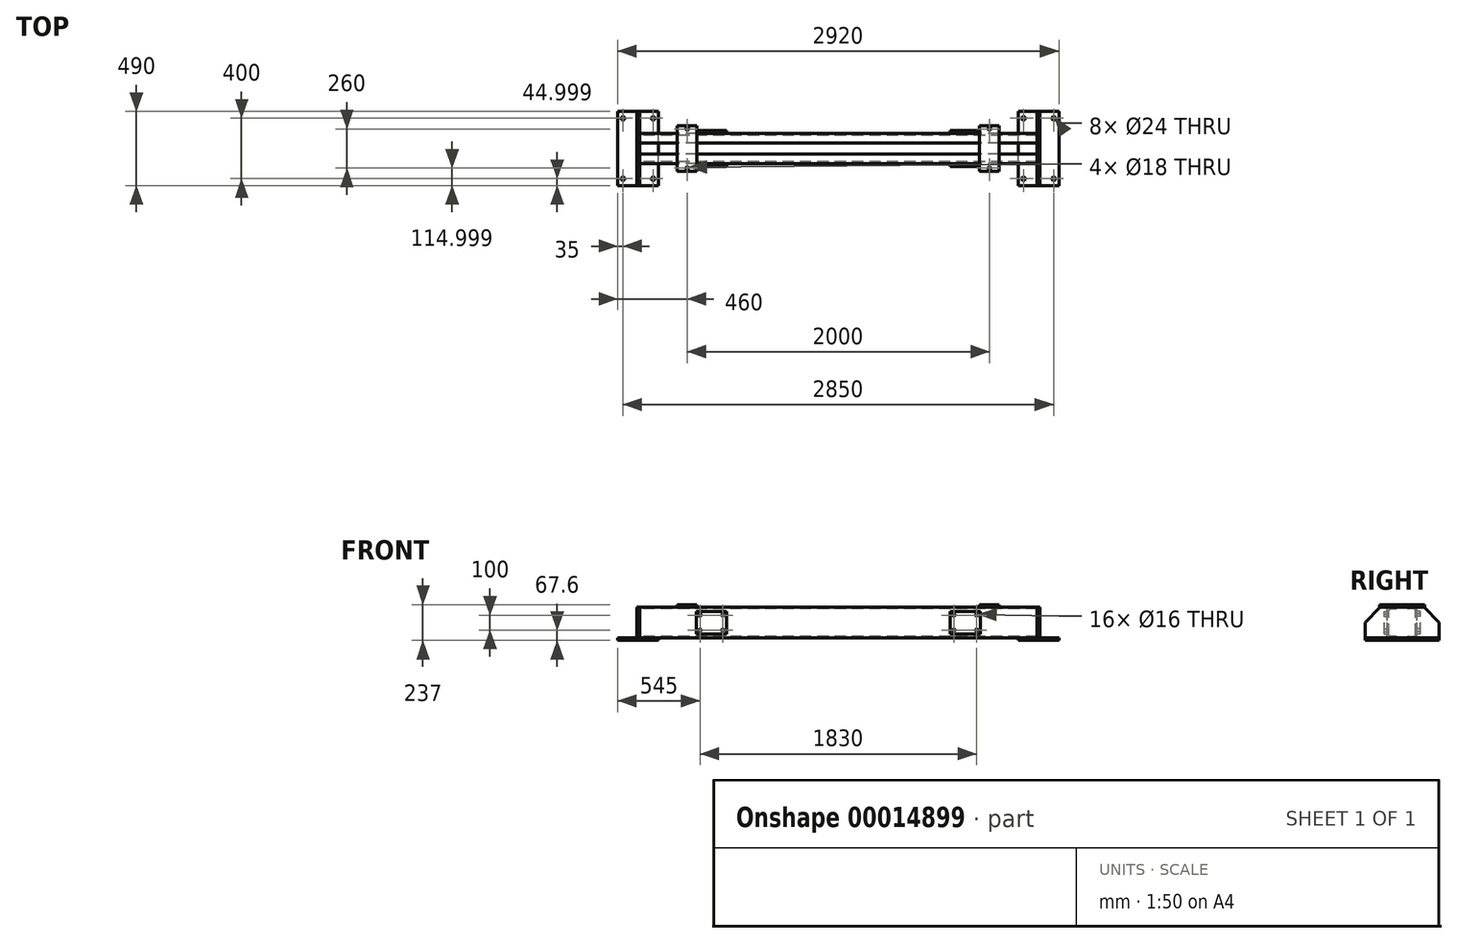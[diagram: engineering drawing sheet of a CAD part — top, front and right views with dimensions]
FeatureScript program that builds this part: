
annotation { "Feature Type Name" : "Feature", "Feature Type Description" : "" }
export const myFeature = defineFeature(function(context is Context, id is Id, definition is map)
    precondition{}
    {
        {
            var Q0;
            Q0=qCreatedBy(makeId("Right.planeOp"),FACE);
            var sketch = newSketch(context, id + "F0", { "sketchPlane" : qUnion([Q0])});
            skLineSegment(sketch, "E0", {"start": v(-32.03, -101.6) * mm, "end": v(-32.03, 101.6) * mm});
            skLineSegment(sketch, "E1", {"start": v(-32.03, 101.6) * mm, "end": v(32.03, 101.6) * mm});
            skLineSegment(sketch, "E2", {"start": v(32.03, 96.65) * mm, "end": v(32.03, 101.6) * mm});
            skArc(sketch, "E3", {"start": v(27.08, 91.7) * mm, "mid": v(30.58, 93.14) * mm, "end": v(32.03, 96.65) * mm});
            skLineSegment(sketch, "E4", {"start": v(-9.46, 91.7) * mm, "end": v(27.08, 91.7) * mm});
            skArc(sketch, "E5", {"start": v(-9.46, 91.7) * mm, "mid": v(-16.64, 88.71) * mm, "end": v(-19.62, 81.53) * mm});
            skLineSegment(sketch, "E6", {"start": v(-19.62, -81.53) * mm, "end": v(-19.62, 81.53) * mm});
            skArc(sketch, "E7", {"start": v(-19.62, -81.53) * mm, "mid": v(-16.64, -88.71) * mm, "end": v(-9.46, -91.7) * mm});
            skLineSegment(sketch, "E8", {"start": v(27.08, -91.7) * mm, "end": v(-9.46, -91.7) * mm});
            skArc(sketch, "E9", {"start": v(32.03, -96.65) * mm, "mid": v(30.58, -93.14) * mm, "end": v(27.08, -91.7) * mm});
            skLineSegment(sketch, "E10", {"start": v(32.03, -101.6) * mm, "end": v(32.03, -96.65) * mm});
            skLineSegment(sketch, "E11", {"start": v(-32.03, -101.6) * mm, "end": v(32.03, -101.6) * mm});
            skSolve(sketch);
        }
        {
            var Q0;
            Q0 = qSketchRegion(id + "F0", true);
            extrude(context, id + "F1", {"entities" : qUnion([Q0]), "endBound" : BoundingType.SYMMETRIC, "depth" : 2631 * mm});
        }
        {
            var Q0;
            Q0=makeQuery(id+"F1.opExtrude","SWEPT_FACE",FACE,{"disambiguationData":[OSD([sQuery(id+"F0.wireOp",EDGE,"E0")])]});
            cPlane(context, id + "F2", {"entities" : qUnion([Q0]), "cplaneType" : CPlaneType.OFFSET, "offset" : 100 * mm, "oppositeDirection" : true, "width" : 150 * mm, "height" : 150 * mm});
        }
        {
            var Q0;
            Q0=makeQuery(id+"F1.opExtrude","SWEPT_BODY",BODY,{"disambiguationData":[OSD([sQuery(id+"F0.wireOp",EDGE,"E0"),sQuery(id+"F0.wireOp",EDGE,"E1"),sQuery(id+"F0.wireOp",EDGE,"E2"),sQuery(id+"F0.wireOp",EDGE,"E3"),sQuery(id+"F0.wireOp",EDGE,"E4"),sQuery(id+"F0.wireOp",EDGE,"E5"),sQuery(id+"F0.wireOp",EDGE,"E6"),sQuery(id+"F0.wireOp",EDGE,"E7"),sQuery(id+"F0.wireOp",EDGE,"E8"),sQuery(id+"F0.wireOp",EDGE,"E9"),sQuery(id+"F0.wireOp",EDGE,"E10"),sQuery(id+"F0.wireOp",EDGE,"E11")])]});
            var Q1;
            Q1=qCreatedBy(id+"F2.planeOp",FACE);
            mirror(context, id + "F3", {"entities" : qUnion([Q0]), "mirrorPlane" : qUnion([Q1])});
        }
        {
            var Q0;
            Q0=makeQuery(id+"F1.opExtrude","CAP_FACE",FACE,{"disambiguationData":[OSD([sQuery(id+"F0.wireOp",EDGE,"E0"),sQuery(id+"F0.wireOp",EDGE,"E1"),sQuery(id+"F0.wireOp",EDGE,"E2"),sQuery(id+"F0.wireOp",EDGE,"E3"),sQuery(id+"F0.wireOp",EDGE,"E4"),sQuery(id+"F0.wireOp",EDGE,"E5"),sQuery(id+"F0.wireOp",EDGE,"E6"),sQuery(id+"F0.wireOp",EDGE,"E7"),sQuery(id+"F0.wireOp",EDGE,"E8"),sQuery(id+"F0.wireOp",EDGE,"E9"),sQuery(id+"F0.wireOp",EDGE,"E10"),sQuery(id+"F0.wireOp",EDGE,"E11")])],"isStart":false});
            var sketch = newSketch(context, id + "F4", { "sketchPlane" : qUnion([Q0])});
            skLineSegment(sketch, "E12.0", {"start": v(167.97, -101.6) * mm, "end": v(167.97, 101.6) * mm, "construction": true});
            skLineSegment(sketch, "E13.0", {"start": v(-32.03, -101.6) * mm, "end": v(-32.03, 101.6) * mm, "construction": true});
            skLineSegment(sketch, "E14", {"start": v(-32.03, 0) * mm, "end": v(167.97, 0) * mm, "construction": true});
            skLineSegment(sketch, "E15", {"start": v(67.97, 0) * mm, "end": v(67.97, -135.85) * mm, "construction": true});
            skLineSegment(sketch, "E16.0.0", {"start": v(-32.03, 101.6) * mm, "end": v(-32.03, -101.6) * mm, "construction": true});
            skLineSegment(sketch, "E16.0.1", {"start": v(-32.03, -101.6) * mm, "end": v(32.03, -101.6) * mm, "construction": true});
            skLineSegment(sketch, "E16.0.2", {"start": v(32.03, -101.6) * mm, "end": v(32.03, -96.65) * mm, "construction": true});
            skArc(sketch, "E16.0.3", {"start": v(32.03, -96.65) * mm, "mid": v(30.58, -93.14) * mm, "end": v(27.08, -91.7) * mm, "construction": true});
            skLineSegment(sketch, "E16.0.4", {"start": v(27.08, -91.7) * mm, "end": v(-9.46, -91.7) * mm, "construction": true});
            skArc(sketch, "E16.0.5", {"start": v(-9.46, -91.7) * mm, "mid": v(-16.64, -88.71) * mm, "end": v(-19.62, -81.53) * mm, "construction": true});
            skLineSegment(sketch, "E16.0.6", {"start": v(-19.62, -81.53) * mm, "end": v(-19.62, 81.53) * mm, "construction": true});
            skArc(sketch, "E16.0.7", {"start": v(-19.62, 81.53) * mm, "mid": v(-16.64, 88.71) * mm, "end": v(-9.46, 91.7) * mm, "construction": true});
            skLineSegment(sketch, "E16.0.8", {"start": v(-9.46, 91.7) * mm, "end": v(27.08, 91.7) * mm, "construction": true});
            skArc(sketch, "E16.0.9", {"start": v(27.08, 91.7) * mm, "mid": v(30.58, 93.14) * mm, "end": v(32.03, 96.65) * mm, "construction": true});
            skLineSegment(sketch, "E16.0.10", {"start": v(32.03, 96.65) * mm, "end": v(32.03, 101.6) * mm, "construction": true});
            skLineSegment(sketch, "E16.0.11", {"start": v(32.03, 101.6) * mm, "end": v(-32.03, 101.6) * mm, "construction": true});
            skLineSegment(sketch, "E17.0.1", {"start": v(167.97, 101.6) * mm, "end": v(103.9, 101.6) * mm, "construction": true});
            skLineSegment(sketch, "E17.0.2", {"start": v(103.9, 101.6) * mm, "end": v(103.9, 96.65) * mm, "construction": true});
            skArc(sketch, "E17.0.3", {"start": v(103.9, 96.65) * mm, "mid": v(105.36, 93.14) * mm, "end": v(108.86, 91.7) * mm, "construction": true});
            skLineSegment(sketch, "E17.0.4", {"start": v(108.86, 91.7) * mm, "end": v(145.4, 91.7) * mm, "construction": true});
            skArc(sketch, "E17.0.5", {"start": v(145.4, 91.7) * mm, "mid": v(152.58, 88.71) * mm, "end": v(155.56, 81.53) * mm, "construction": true});
            skLineSegment(sketch, "E17.0.6", {"start": v(155.56, 81.53) * mm, "end": v(155.56, -81.53) * mm, "construction": true});
            skArc(sketch, "E17.0.7", {"start": v(155.56, -81.53) * mm, "mid": v(152.58, -88.71) * mm, "end": v(145.4, -91.7) * mm, "construction": true});
            skLineSegment(sketch, "E17.0.8", {"start": v(145.4, -91.7) * mm, "end": v(108.86, -91.7) * mm, "construction": true});
            skArc(sketch, "E17.0.9", {"start": v(108.86, -91.7) * mm, "mid": v(105.36, -93.14) * mm, "end": v(103.9, -96.65) * mm, "construction": true});
            skLineSegment(sketch, "E17.0.10", {"start": v(103.9, -96.65) * mm, "end": v(103.9, -101.6) * mm, "construction": true});
            skLineSegment(sketch, "E17.0.11", {"start": v(103.9, -101.6) * mm, "end": v(167.97, -101.6) * mm, "construction": true});
            skLineSegment(sketch, "E18.0", {"start": v(-177.03, 0) * mm, "end": v(-177.03, -101.6) * mm, "construction": true});
            skLineSegment(sketch, "E19.MirrorCS", {"start": v(312.97, 101.6) * mm, "end": v(312.97, -101.6) * mm});
            skPoint(sketch, "E20.orphan", {"position": v(312.97, 0) * mm});
            skLineSegment(sketch, "E21.bottom", {"start": v(312.97, 101.6) * mm, "end": v(-177.03, 101.6) * mm});
            skLineSegment(sketch, "E21.top", {"start": v(312.97, -101.6) * mm, "end": v(-177.03, -101.6) * mm});
            skLineSegment(sketch, "E21.right", {"start": v(-177.03, 101.6) * mm, "end": v(-177.03, -101.6) * mm});
            skSolve(sketch);
        }
        {
            var Q0;
            Q0 = qSketchRegion(id + "F4", true);
            extrude(context, id + "F5", {"entities" : qUnion([Q0]), "depth" : 19 * mm});
        }
        {
            var Q0;
            Q0=makeQuery(id+"F5.opExtrude","SWEPT_EDGE",EDGE,{"disambiguationData":[OSD([sQuery(id+"F4.wireOp",EDGE,"E21.bottom"),sQuery(id+"F4.wireOp",EDGE,"E21.right")])]});
            var Q1;
            Q1=makeQuery(id+"F5.opExtrude","SWEPT_EDGE",EDGE,{"disambiguationData":[OSD([sQuery(id+"F4.wireOp",EDGE,"E21.bottom"),sQuery(id+"F4.wireOp",EDGE,"E19.MirrorCS")])]});
            chamfer(context, id + "F6", {"entities" : qUnion([Q0, Q1]), "width" : 100 * mm, "tangentPropagation" : true});
        }
        {
            var Q0;
            Q0=makeQuery(id+"F5.opExtrude","SWEPT_BODY",BODY,{"disambiguationData":[OSD([sQuery(id+"F4.wireOp",EDGE,"E21.bottom"),sQuery(id+"F4.wireOp",EDGE,"E21.top"),sQuery(id+"F4.wireOp",EDGE,"E19.MirrorCS"),sQuery(id+"F4.wireOp",EDGE,"E21.right")])]});
            var Q1;
            Q1=qCreatedBy(makeId("Right.planeOp"),FACE);
            mirror(context, id + "F7", {"entities" : qUnion([Q0]), "mirrorPlane" : qUnion([Q1])});
        }
        {
            var Q0;
            Q0=makeQuery(id+"F7.opPattern","COPY",FACE,{"derivedFrom":makeQuery(id+"F5.opExtrude","SWEPT_FACE",FACE,{"disambiguationData":[OSD([sQuery(id+"F4.wireOp",EDGE,"E21.top")])]}),"instanceName":"1"});
            var sketch = newSketch(context, id + "F8", { "sketchPlane" : qUnion([Q0])});
            skLineSegment(sketch, "E22", {"start": v(-1325, 177.03) * mm, "end": v(-1325, -312.97) * mm, "construction": true});
            skLineSegment(sketch, "E23.0", {"start": v(-1460, 177.03) * mm, "end": v(-1460, -312.97) * mm});
            skLineSegment(sketch, "E24", {"start": v(-1460, 177.03) * mm, "end": v(-1325, 177.03) * mm});
            skLineSegment(sketch, "E25", {"start": v(-1460, -312.97) * mm, "end": v(-1325, -312.97) * mm});
            skLineSegment(sketch, "E26.MirrorCS", {"start": v(-1190, 177.03) * mm, "end": v(-1325, 177.03) * mm});
            skLineSegment(sketch, "E27.MirrorCS", {"start": v(-1190, 177.03) * mm, "end": v(-1190, -312.97) * mm});
            skLineSegment(sketch, "E28.MirrorCS", {"start": v(-1190, -312.97) * mm, "end": v(-1325, -312.97) * mm});
            skLineSegment(sketch, "E29", {"start": v(-1190, -67.97) * mm, "end": v(-1460, -67.97) * mm, "construction": true});
            skLineSegment(sketch, "E30.0", {"start": v(-1425, 177.03) * mm, "end": v(-1425, -312.97) * mm, "construction": true});
            skLineSegment(sketch, "E31.0", {"start": v(-1190, -267.97) * mm, "end": v(-1460, -267.97) * mm, "construction": true});
            skCircle(sketch, "E32", {"center": v(-1425, -267.97) * mm, "radius": 12 * mm});
            skCircle(sketch, "E33.MirrorC", {"center": v(-1225, -267.97) * mm, "radius": 12 * mm});
            skCircle(sketch, "E34.MirrorC", {"center": v(-1225, 132.03) * mm, "radius": 12 * mm});
            skCircle(sketch, "E35.MirrorC", {"center": v(-1425, 132.03) * mm, "radius": 12 * mm});
            skSolve(sketch);
        }
        {
            var Q0;
            Q0 = qSketchRegion(id + "F8", true);
            extrude(context, id + "F9", {"entities" : qUnion([Q0]), "depth" : 16 * mm});
        }
        {
            var Q0;
            Q0=makeQuery(id+"F9.opExtrude","SWEPT_BODY",BODY,{"disambiguationData":[OSD([sQuery(id+"F8.wireOp",EDGE,"E23.0"),sQuery(id+"F8.wireOp",EDGE,"E24"),sQuery(id+"F8.wireOp",EDGE,"E25"),sQuery(id+"F8.wireOp",EDGE,"E26.MirrorCS"),sQuery(id+"F8.wireOp",EDGE,"E27.MirrorCS"),sQuery(id+"F8.wireOp",EDGE,"E28.MirrorCS"),sQuery(id+"F8.wireOp",EDGE,"E32"),sQuery(id+"F8.wireOp",EDGE,"E33.MirrorC"),sQuery(id+"F8.wireOp",EDGE,"E34.MirrorC"),sQuery(id+"F8.wireOp",EDGE,"E35.MirrorC")])]});
            var Q1;
            Q1=qCreatedBy(makeId("Right.planeOp"),FACE);
            mirror(context, id + "F10", {"entities" : qUnion([Q0]), "mirrorPlane" : qUnion([Q1])});
        }
        {
            var Q0;
            Q0=makeQuery(id+"F1.opExtrude","SWEPT_FACE",FACE,{"disambiguationData":[OSD([sQuery(id+"F0.wireOp",EDGE,"E1")])]});
            var sketch = newSketch(context, id + "F11", { "sketchPlane" : qUnion([Q0])});
            skLineSegment(sketch, "E36.0", {"start": v(-1334.5, 212.97) * mm, "end": v(-1334.5, -77.03) * mm});
            skLineSegment(sketch, "E37", {"start": v(-1334.5, 67.97) * mm, "end": v(-259.57, 67.97) * mm, "construction": true});
            skLineSegment(sketch, "E38", {"start": v(0, 0) * mm, "end": v(0, 384.06) * mm, "construction": true});
            skLineSegment(sketch, "E39.0", {"start": v(-1000, 0) * mm, "end": v(-1000, 384.06) * mm, "construction": true});
            skLineSegment(sketch, "E40.0", {"start": v(-1065, 217.97) * mm, "end": v(-1000, 217.97) * mm});
            skLineSegment(sketch, "E41.0", {"start": v(-1065, 67.97) * mm, "end": v(-1065, 217.97) * mm});
            skLineSegment(sketch, "E42.MirrorCS", {"start": v(-935, 217.97) * mm, "end": v(-1000, 217.97) * mm});
            skLineSegment(sketch, "E43.MirrorCS", {"start": v(-935, 67.97) * mm, "end": v(-935, 217.97) * mm});
            skLineSegment(sketch, "E44.MirrorCS", {"start": v(-1065, 67.97) * mm, "end": v(-1065, -82.03) * mm});
            skLineSegment(sketch, "E45.MirrorCS", {"start": v(-1065, -82.03) * mm, "end": v(-1000, -82.03) * mm});
            skLineSegment(sketch, "E46.MirrorCS", {"start": v(-935, -82.03) * mm, "end": v(-1000, -82.03) * mm});
            skLineSegment(sketch, "E47.MirrorCS", {"start": v(-935, 67.97) * mm, "end": v(-935, -82.03) * mm});
            skLineSegment(sketch, "E48.0", {"start": v(-1075, 0) * mm, "end": v(-1075, 384.06) * mm, "construction": true});
            skLineSegment(sketch, "E49.0", {"start": v(-1334.5, 197.97) * mm, "end": v(-259.57, 197.97) * mm, "construction": true});
            skCircle(sketch, "E50", {"center": v(-1000, 197.97) * mm, "radius": 9 * mm});
            skCircle(sketch, "E51.MirrorC", {"center": v(-1000, -62.03) * mm, "radius": 9 * mm});
            skSolve(sketch);
        }
        {
            var Q0;
            Q0 = qSketchRegion(id + "F11", true);
            extrude(context, id + "F12", {"entities" : qUnion([Q0]), "depth" : 17.8 * mm});
        }
        {
            var Q0;
            Q0=makeQuery(id+"F12.opExtrude","SWEPT_BODY",BODY,{"disambiguationData":[OSD([sQuery(id+"F11.wireOp",EDGE,"E40.0"),sQuery(id+"F11.wireOp",EDGE,"E41.0"),sQuery(id+"F11.wireOp",EDGE,"E42.MirrorCS"),sQuery(id+"F11.wireOp",EDGE,"E43.MirrorCS"),sQuery(id+"F11.wireOp",EDGE,"E44.MirrorCS"),sQuery(id+"F11.wireOp",EDGE,"E45.MirrorCS"),sQuery(id+"F11.wireOp",EDGE,"E46.MirrorCS"),sQuery(id+"F11.wireOp",EDGE,"E47.MirrorCS"),sQuery(id+"F11.wireOp",EDGE,"E50"),sQuery(id+"F11.wireOp",EDGE,"E51.MirrorC")])]});
            var Q1;
            Q1=qCreatedBy(makeId("Right.planeOp"),FACE);
            mirror(context, id + "F13", {"entities" : qUnion([Q0]), "mirrorPlane" : qUnion([Q1])});
        }
        {
            var Q0;
            Q0=makeQuery(id+"F1.opExtrude","SWEPT_FACE",FACE,{"disambiguationData":[OSD([sQuery(id+"F0.wireOp",EDGE,"E0")])]});
            var sketch = newSketch(context, id + "F14", { "sketchPlane" : qUnion([Q0])});
            skLineSegment(sketch, "E52", {"start": v(0, 312.61) * mm, "end": v(0, -357) * mm, "construction": true});
            skLineSegment(sketch, "E53", {"start": v(-1498.31, 0) * mm, "end": v(1831.27, 0) * mm, "construction": true});
            skLineSegment(sketch, "E54.0", {"start": v(-840, 312.61) * mm, "end": v(-840, -357) * mm, "construction": true});
            skLineSegment(sketch, "E55.0", {"start": v(-1498.31, -75) * mm, "end": v(1831.27, -75) * mm, "construction": true});
            skLineSegment(sketch, "E56.0", {"start": v(-940, 312.61) * mm, "end": v(-940, -357) * mm, "construction": true});
            skLineSegment(sketch, "E57.bottom", {"start": v(-940, -75) * mm, "end": v(-740, -75) * mm});
            skLineSegment(sketch, "E57.top", {"start": v(-940, 75) * mm, "end": v(-740, 75) * mm});
            skLineSegment(sketch, "E57.left", {"start": v(-940, -75) * mm, "end": v(-940, 75) * mm});
            skLineSegment(sketch, "E57.right", {"start": v(-740, -75) * mm, "end": v(-740, 75) * mm});
            skLineSegment(sketch, "E58.0", {"start": v(-915, 312.61) * mm, "end": v(-915, -357) * mm, "construction": true});
            skLineSegment(sketch, "E59.0", {"start": v(-1498.31, -50) * mm, "end": v(1831.27, -50) * mm, "construction": true});
            skCircle(sketch, "E60", {"center": v(-915, -50) * mm, "radius": 8 * mm});
            skCircle(sketch, "E61.MirrorC", {"center": v(-915, 50) * mm, "radius": 8 * mm});
            skCircle(sketch, "E62.MirrorC", {"center": v(-765, 50) * mm, "radius": 8 * mm});
            skCircle(sketch, "E63.MirrorC", {"center": v(-765, -50) * mm, "radius": 8 * mm});
            skSolve(sketch);
        }
        {
            var Q0;
            Q0 = qSketchRegion(id + "F14", true);
            extrude(context, id + "F15", {"entities" : qUnion([Q0]), "depth" : 19 * mm});
        }
        {
            var Q0;
            Q0=makeQuery(id+"F15.opExtrude","SWEPT_BODY",BODY,{"disambiguationData":[OSD([sQuery(id+"F14.wireOp",EDGE,"E57.bottom"),sQuery(id+"F14.wireOp",EDGE,"E57.top"),sQuery(id+"F14.wireOp",EDGE,"E57.left"),sQuery(id+"F14.wireOp",EDGE,"E57.right"),sQuery(id+"F14.wireOp",EDGE,"E60"),sQuery(id+"F14.wireOp",EDGE,"E61.MirrorC"),sQuery(id+"F14.wireOp",EDGE,"E62.MirrorC"),sQuery(id+"F14.wireOp",EDGE,"E63.MirrorC")])]});
            var Q1;
            Q1=qCreatedBy(makeId("Right.planeOp"),FACE);
            mirror(context, id + "F16", {"entities" : qUnion([Q0]), "mirrorPlane" : qUnion([Q1])});
        }
        {
            var Q0;
            Q0=makeQuery(id+"F15.opExtrude","SWEPT_BODY",BODY,{"disambiguationData":[OSD([sQuery(id+"F14.wireOp",EDGE,"E57.bottom"),sQuery(id+"F14.wireOp",EDGE,"E57.top"),sQuery(id+"F14.wireOp",EDGE,"E57.left"),sQuery(id+"F14.wireOp",EDGE,"E57.right"),sQuery(id+"F14.wireOp",EDGE,"E60"),sQuery(id+"F14.wireOp",EDGE,"E61.MirrorC"),sQuery(id+"F14.wireOp",EDGE,"E62.MirrorC"),sQuery(id+"F14.wireOp",EDGE,"E63.MirrorC")])]});
            var Q1;
            Q1=makeQuery(id+"F16.opPattern","COPY",BODY,{"derivedFrom":makeQuery(id+"F15.opExtrude","SWEPT_BODY",BODY,{"disambiguationData":[OSD([sQuery(id+"F14.wireOp",EDGE,"E57.bottom"),sQuery(id+"F14.wireOp",EDGE,"E57.top"),sQuery(id+"F14.wireOp",EDGE,"E57.left"),sQuery(id+"F14.wireOp",EDGE,"E57.right"),sQuery(id+"F14.wireOp",EDGE,"E60"),sQuery(id+"F14.wireOp",EDGE,"E61.MirrorC"),sQuery(id+"F14.wireOp",EDGE,"E62.MirrorC"),sQuery(id+"F14.wireOp",EDGE,"E63.MirrorC")])]}),"instanceName":"1"});
            var Q2;
            Q2=qCreatedBy(id+"F2.planeOp",FACE);
            mirror(context, id + "F17", {"entities" : qUnion([Q0, Q1]), "mirrorPlane" : qUnion([Q2])});
        }
    });
